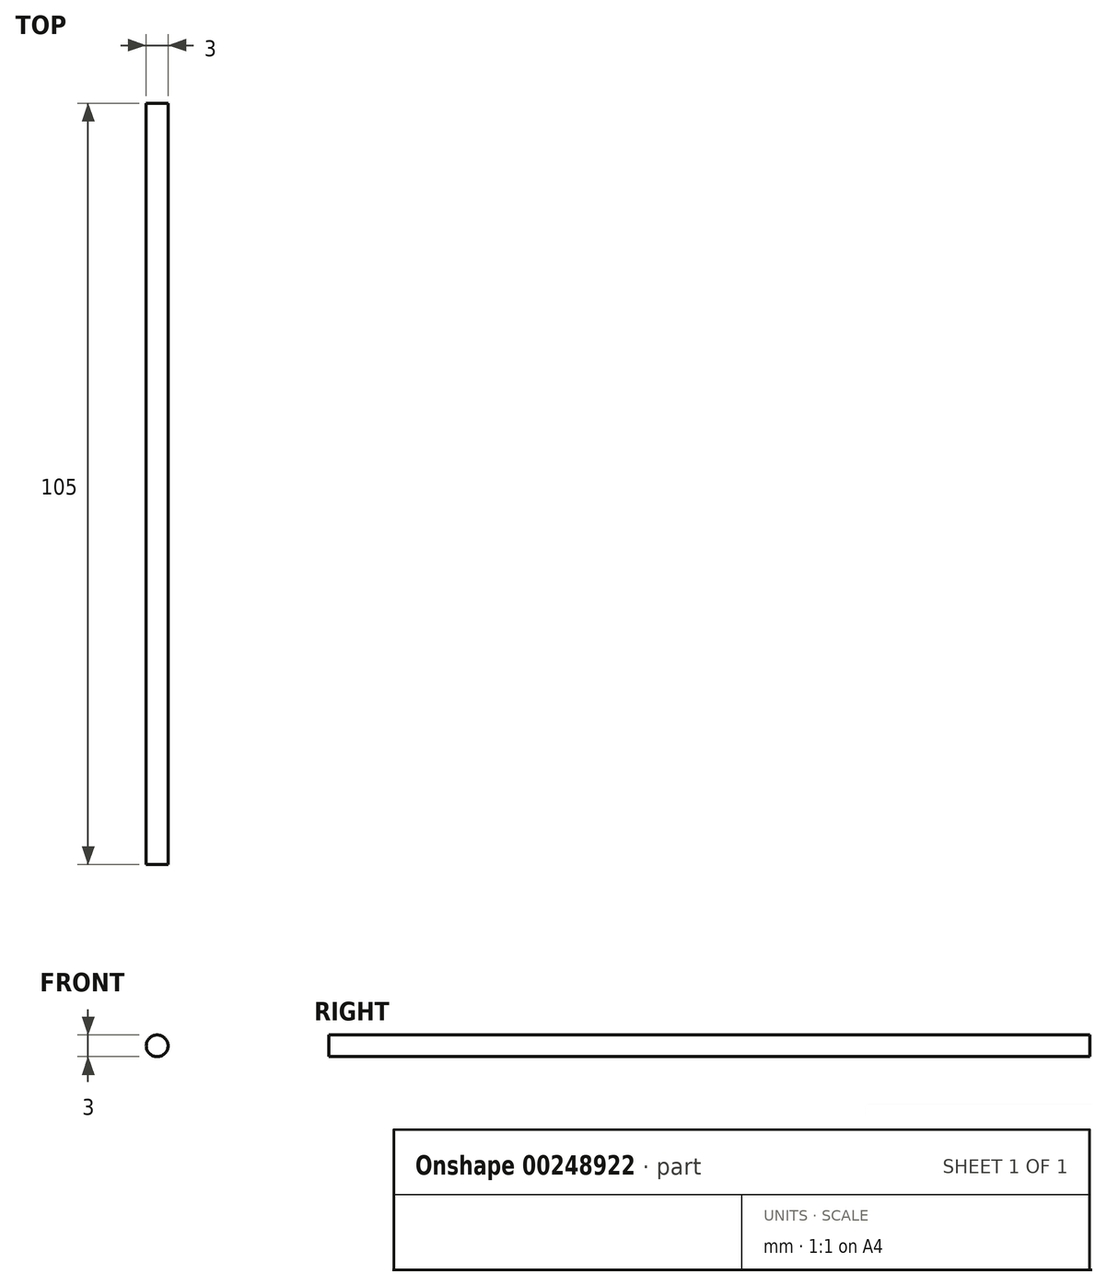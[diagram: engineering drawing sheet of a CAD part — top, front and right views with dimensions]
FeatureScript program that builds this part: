
annotation { "Feature Type Name" : "Feature", "Feature Type Description" : "" }
export const myFeature = defineFeature(function(context is Context, id is Id, definition is map)
    precondition{}
    {
        {
            var Q0;
            Q0=qCreatedBy(makeId("Front.planeOp"),FACE);
            var sketch = newSketch(context, id + "F0", { "sketchPlane" : qUnion([Q0])});
            skCircle(sketch, "E0", {"center": v(18.68, 12.5) * mm, "radius": 1.5 * mm});
            skSolve(sketch);
        }
        {
            var Q0;
            Q0=makeQuery(id+"F0.imprint","IMPRINT",FACE,{"disambiguationData":[TD([[makeQuery(id+"F0.imprint","IMPRINT",EDGE,{"derivedFrom":sQuery(id+"F0.wireOp",EDGE,"E0")}),1.0]])]});
            extrude(context, id + "F1", {"entities" : qUnion([Q0]), "depth" : 105 * mm});
        }
    });
